# Revit family: Building-ContenitoriIncasso-GEWISS-24SC-GREENWALL-SCATOLE-INCASSO_3P
name_source: partatom
category: Apparecchi elettrici
revit_build: Autodesk Revit 2016 (Build: 20161004_0715(x64)
units: mm (PartAtom-declared; Revit-internal decimal feet)

## family parameters
Condiviso = Sì
Host = Superficie
Mantenere orientamento annotazione = Sì
Numero OmniClass = 23.80.30.14.24
Punto di calcolo locali = Sì
Quota connettore circolare = Usa diametro
Taglio con vuoti quando caricato = Sì
Tipo di parte = Normale
Titolo OmniClass = Junction Boxes

## types (1)
- GW24403PM - Halogen free - 3P
    Catalogo = BUILDING
    Catalogo Serie = 24SC
    Codice EAN = 8011564801912
    Codice Electrocod = 0210
    Descrizione = SCATOLA 3P.PARETI MOBILI-LEGGERE GREEN
    Descrizione: = 3 posti
    GW - Caratteristiche = Halogen free
    GW - Dim. esterne BxHxP (mm) = 110x73x50
    GW - Installazione = Incasso
    GW - Interasse fissaggio supporti = 83,5MM
    GW - N. moduli SYSTEM = 3 posti
    GW - Per Pareti = Cartongesso
    GW - Predisposizione scomparti = 2
    GW - Temperatura di impiego = -15 +60 °C
    GW - Tipo Materiale = Halogen free secondo norma EN 50267-2-2
    Glow Wire Test = 850°C
    Grado di protezione = IP40
    IDF = a35ff123-51a4-436c-acec-84fbbce8256b
    IDT = 7e9ebd6a-1061-4bfe-9397-917a2868acc8
    Immagine tipo = GW24403PM.jpg
    Modello = GW24403PM
    Produttore = GEWISS S.p.A.
    Prospetto di default = 1219 mm
    Resistenza agli urti = IK07
    SEO = Scatola
    Scheda Tecnica = https://www.gewiss.com
    Termopressione con biglia = 70 °C
    Tipo: = Alta capienza
    URL = https://www.gewiss.com
    Versione file RFA = 19.0

## geometry (parser evidence)
native form markers: Blend x4, Sweep x3
no freeform markers — native parametric forms only
